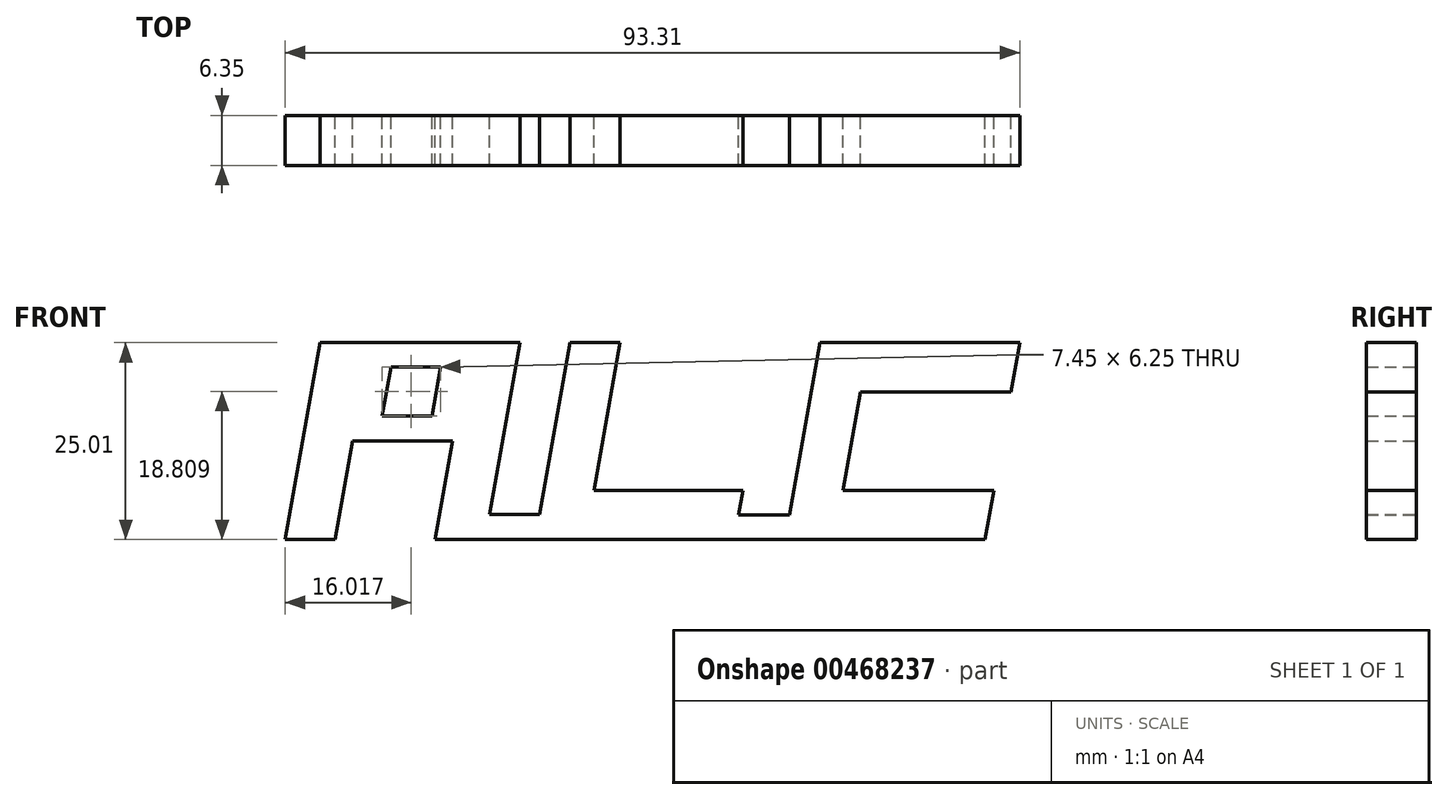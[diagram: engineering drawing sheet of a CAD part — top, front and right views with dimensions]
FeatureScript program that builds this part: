
annotation { "Feature Type Name" : "Feature", "Feature Type Description" : "" }
export const myFeature = defineFeature(function(context is Context, id is Id, definition is map)
    precondition{}
    {
        {
            var Q0;
            Q0=qCreatedBy(makeId("Front.planeOp"),FACE);
            var sketch = newSketch(context, id + "F0", { "sketchPlane" : qUnion([Q0])});
            skLineSegment(sketch, "E0", {"start": v(0, 0) * mm, "end": v(4.41, 25.01) * mm});
            skLineSegment(sketch, "E1", {"start": v(0, 0) * mm, "end": v(0, 26.96) * mm});
            skLineSegment(sketch, "E2", {"start": v(4.41, 25.01) * mm, "end": v(29.81, 25.01) * mm});
            skLineSegment(sketch, "E3", {"start": v(29.81, 25.01) * mm, "end": v(25.4, 0) * mm});
            skLineSegment(sketch, "E4", {"start": v(0, 0) * mm, "end": v(6.35, 0) * mm});
            skLineSegment(sketch, "E5", {"start": v(6.35, 0) * mm, "end": v(8.56, 12.5) * mm});
            skLineSegment(sketch, "E6", {"start": v(8.56, 12.5) * mm, "end": v(21.26, 12.5) * mm});
            skLineSegment(sketch, "E7", {"start": v(21.26, 12.5) * mm, "end": v(19.05, 0) * mm});
            skLineSegment(sketch, "E8", {"start": v(19.05, 0) * mm, "end": v(25.4, 0) * mm});
            skLineSegment(sketch, "E9", {"start": v(14.9, 12.5) * mm, "end": v(17.11, 25.01) * mm});
            skLineSegment(sketch, "E10", {"start": v(15.47, 15.68) * mm, "end": v(18.64, 15.68) * mm});
            skLineSegment(sketch, "E11", {"start": v(18.64, 15.68) * mm, "end": v(19.74, 21.94) * mm});
            skLineSegment(sketch, "E12", {"start": v(19.74, 21.94) * mm, "end": v(13.43, 21.94) * mm});
            skLineSegment(sketch, "E13", {"start": v(15.47, 15.68) * mm, "end": v(12.3, 15.68) * mm});
            skLineSegment(sketch, "E14", {"start": v(12.3, 15.68) * mm, "end": v(13.43, 21.94) * mm});
            skLineSegment(sketch, "E15", {"start": v(29.81, 25.01) * mm, "end": v(42.51, 25.01) * mm});
            skLineSegment(sketch, "E16", {"start": v(42.51, 25.01) * mm, "end": v(38.1, 0) * mm});
            skLineSegment(sketch, "E17", {"start": v(25.4, 0) * mm, "end": v(63.5, 0) * mm});
            skLineSegment(sketch, "E18", {"start": v(63.5, 0) * mm, "end": v(64.6, 6.25) * mm});
            skLineSegment(sketch, "E19", {"start": v(64.6, 6.25) * mm, "end": v(39.2, 6.25) * mm});
            skLineSegment(sketch, "E20", {"start": v(64.6, 6.25) * mm, "end": v(67.91, 25.01) * mm});
            skLineSegment(sketch, "E21", {"start": v(67.91, 25.01) * mm, "end": v(93.31, 25.01) * mm});
            skLineSegment(sketch, "E22", {"start": v(93.31, 25.01) * mm, "end": v(92.2, 18.76) * mm});
            skLineSegment(sketch, "E23", {"start": v(88.9, 0) * mm, "end": v(63.5, 0) * mm});
            skLineSegment(sketch, "E24", {"start": v(70.85, 6.25) * mm, "end": v(83.55, 6.25) * mm});
            skLineSegment(sketch, "E25", {"start": v(85.76, 18.76) * mm, "end": v(73.06, 18.76) * mm});
            skLineSegment(sketch, "E26", {"start": v(73.06, 18.76) * mm, "end": v(70.85, 6.25) * mm});
            skLineSegment(sketch, "E27", {"start": v(83.55, 6.25) * mm, "end": v(90, 6.25) * mm});
            skLineSegment(sketch, "E28", {"start": v(85.76, 18.76) * mm, "end": v(92.2, 18.76) * mm});
            skLineSegment(sketch, "E29.trimOffspring", {"start": v(90, 6.25) * mm, "end": v(88.9, 0) * mm});
            skLineSegment(sketch, "E30", {"start": v(36.16, 25.01) * mm, "end": v(31.75, 0) * mm});
            skLineSegment(sketch, "E31", {"start": v(32.3, 3.17) * mm, "end": v(25.96, 3.17) * mm});
            skLineSegment(sketch, "E32", {"start": v(58.15, 6.25) * mm, "end": v(57.05, 0) * mm});
            skLineSegment(sketch, "E33", {"start": v(57.6, 3.13) * mm, "end": v(64.05, 3.13) * mm});
            skSolve(sketch);
        }
        {
            var Q0;
            {var subQ5=sQuery(id+"F0.wireOp",EDGE,"E33");Q0=makeQuery(id+"F0.imprint","IMPRINT",FACE,{"disambiguationData":[TD([[makeQuery(id+"F0.imprint","IMPRINT",EDGE,{"derivedFrom":subQ5}),-1.0]])]});}
            var Q1;
            {var subQ3=sQuery(id+"F0.wireOp",EDGE,"E20");Q1=makeQuery(id+"F0.imprint","IMPRINT",FACE,{"disambiguationData":[TD([[makeQuery(id+"F0.imprint","IMPRINT",EDGE,{"derivedFrom":subQ3}),-1.0]])]});}
            var Q2;
            {var subQ6=sQuery(id+"F0.wireOp",EDGE,"E0");Q2=makeQuery(id+"F0.imprint","IMPRINT",FACE,{"disambiguationData":[TD([[makeQuery(id+"F0.imprint","IMPRINT",EDGE,{"derivedFrom":subQ6}),-1.0]])]});}
            var Q3;
            {var subQ1=sQuery(id+"F0.wireOp",EDGE,"E16");var subQ6=sQuery(id+"F0.wireOp",EDGE,"E15");var subQ7=makeQuery(id+"F0.imprint","INTERSECT",VERTEX,{"derivedFrom":[subQ6,subQ1]});Q3=makeQuery(id+"F0.imprint","IMPRINT",FACE,{"disambiguationData":[TD([[makeQuery(id+"F0.imprint","IMPRINT",EDGE,{"disambiguationData":[TD([[subQ7,1.0]])],"derivedFrom":subQ6}),-1.0]])]});}
            var Q4;
            {var subQ5=sQuery(id+"F0.wireOp",EDGE,"E7");Q4=makeQuery(id+"F0.imprint","IMPRINT",FACE,{"disambiguationData":[TD([[makeQuery(id+"F0.imprint","IMPRINT",EDGE,{"derivedFrom":subQ5}),1.0]])]});}
            var Q5;
            {var subQ3=sQuery(id+"F0.wireOp",EDGE,"E31");Q5=makeQuery(id+"F0.imprint","IMPRINT",FACE,{"disambiguationData":[TD([[makeQuery(id+"F0.imprint","IMPRINT",EDGE,{"derivedFrom":subQ3}),1.0]])]});}
            var Q6;
            {var subQ4=sQuery(id+"F0.wireOp",EDGE,"E17");var subQ5=sQuery(id+"F0.wireOp",EDGE,"E16");var subQ6=makeQuery(id+"F0.imprint","INTERSECT",VERTEX,{"derivedFrom":[subQ5,subQ4]});Q6=makeQuery(id+"F0.imprint","IMPRINT",FACE,{"disambiguationData":[TD([[makeQuery(id+"F0.imprint","IMPRINT",EDGE,{"disambiguationData":[TD([[subQ6,1.0]])],"derivedFrom":subQ5}),1.0]])]});}
            extrude(context, id + "F1", {"entities" : qUnion([Q0, Q1, Q2, Q3, Q4, Q5, Q6]), "depth" : 6.35 * mm});
        }
    });
